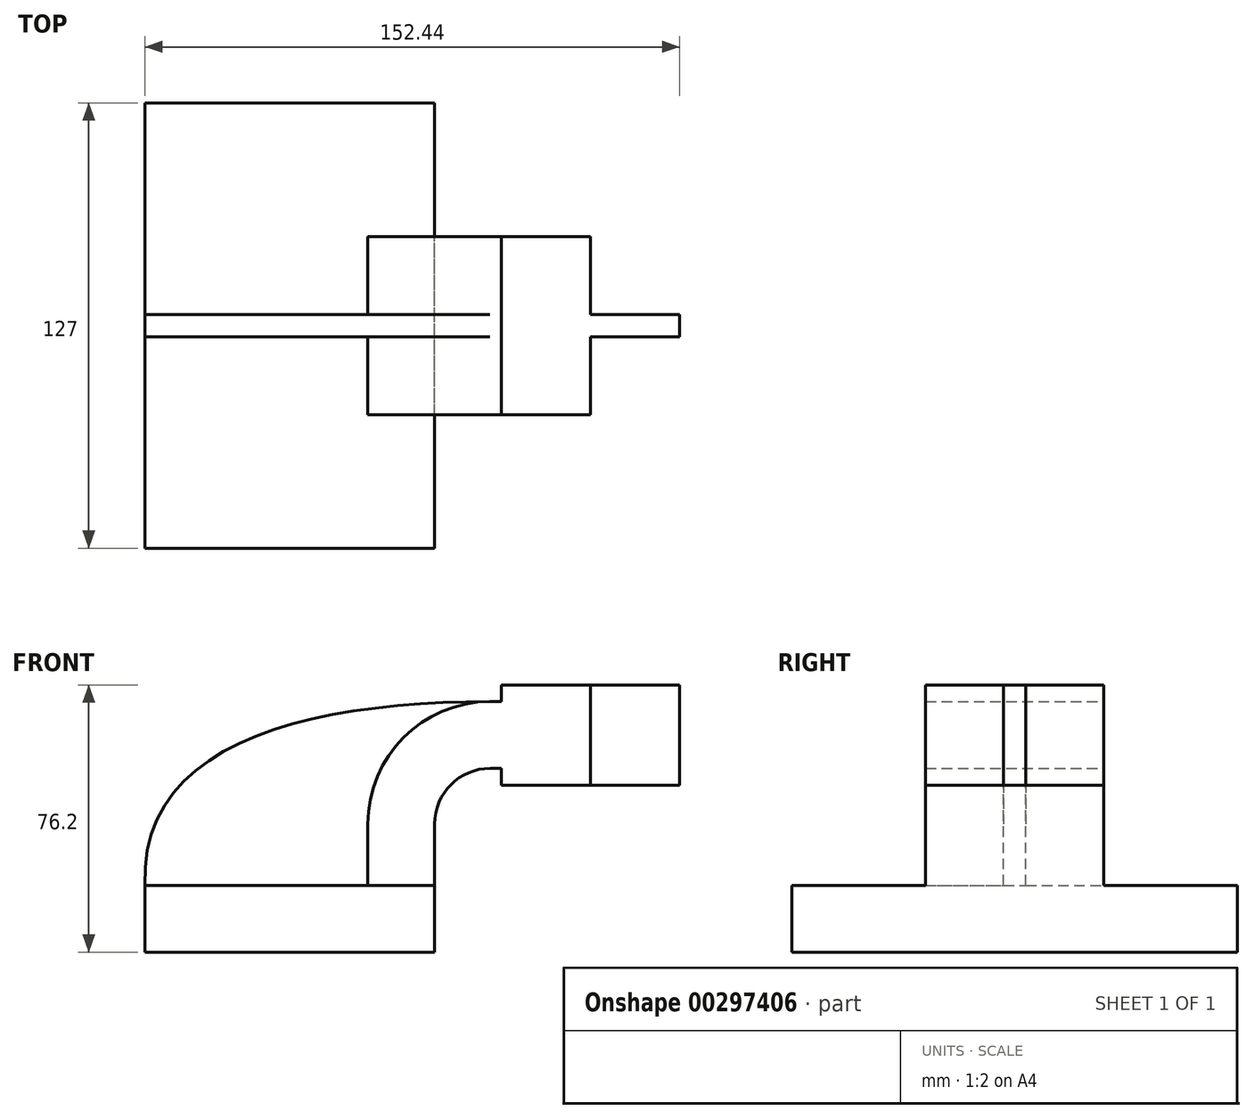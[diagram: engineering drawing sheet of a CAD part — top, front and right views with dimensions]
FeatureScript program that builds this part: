
annotation { "Feature Type Name" : "Feature", "Feature Type Description" : "" }
export const myFeature = defineFeature(function(context is Context, id is Id, definition is map)
    precondition{}
    {
        {
            var Q0;
            Q0=qCreatedBy(makeId("Front.planeOp"),FACE);
            var sketch = newSketch(context, id + "F0", { "sketchPlane" : qUnion([Q0])});
            skLineSegment(sketch, "E0.bottom", {"start": v(41.28, 9.53) * mm, "end": v(-41.28, 9.53) * mm});
            skLineSegment(sketch, "E0.top", {"start": v(41.28, -9.53) * mm, "end": v(-41.28, -9.53) * mm});
            skLineSegment(sketch, "E0.left", {"start": v(41.28, 9.53) * mm, "end": v(41.28, -9.53) * mm});
            skLineSegment(sketch, "E0.right", {"start": v(-41.28, 9.53) * mm, "end": v(-41.28, -9.53) * mm});
            skPoint(sketch, "E0.middle", {"position": v(0, 0) * mm});
            skLineSegment(sketch, "E1.bottom", {"start": v(111.12, 38.1) * mm, "end": v(60.33, 38.1) * mm});
            skLineSegment(sketch, "E1.top", {"start": v(111.13, 66.67) * mm, "end": v(60.33, 66.67) * mm});
            skLineSegment(sketch, "E1.left", {"start": v(111.12, 38.1) * mm, "end": v(111.12, 66.68) * mm});
            skLineSegment(sketch, "E1.right", {"start": v(60.33, 38.1) * mm, "end": v(60.33, 66.68) * mm});
            skPoint(sketch, "E1.middle", {"position": v(85.73, 52.39) * mm});
            skLineSegment(sketch, "E2", {"start": v(41.28, 9.53) * mm, "end": v(41.28, 27) * mm});
            skArc(sketch, "E3", {"start": v(41.28, 27) * mm, "mid": v(45.92, 38.23) * mm, "end": v(57.15, 42.88) * mm});
            skLineSegment(sketch, "E4", {"start": v(57.15, 42.88) * mm, "end": v(85.73, 42.88) * mm});
            skLineSegment(sketch, "E5.0", {"start": v(57.15, 61.93) * mm, "end": v(85.73, 61.93) * mm});
            skArc(sketch, "E5.1", {"start": v(22.23, 27) * mm, "mid": v(32.45, 51.7) * mm, "end": v(57.15, 61.93) * mm});
            skLineSegment(sketch, "E5.2", {"start": v(22.23, 9.53) * mm, "end": v(22.23, 27) * mm});
            skLineSegment(sketch, "E6", {"start": v(85.73, 38.1) * mm, "end": v(85.73, 66.67) * mm});
            skFitSpline(sketch, "E7", {"points": [v(-41.28, 9.52) * mm, v(57.15, 61.93) * mm], "startDerivative": vector(-5.3, 122.94) * mm, "endDerivative": vector(154.34, 0.3) * mm});
            skSolve(sketch);
        }
        {
            var Q0;
            Q0=makeQuery(id+"F0.imprint","IMPRINT",FACE,{"disambiguationData":[TD([[makeQuery(id+"F0.imprint","IMPRINT",EDGE,{"derivedFrom":sQuery(id+"F0.wireOp",EDGE,"E0.top")}),-1.0]])]});
            extrude(context, id + "F1", {"entities" : qUnion([Q0]), "endBound" : BoundingType.SYMMETRIC, "depth" : 127 * mm});
        }
        {
            var Q0;
            {var subQ1=sQuery(id+"F0.wireOp",EDGE,"E2");Q0=makeQuery(id+"F0.imprint","IMPRINT",FACE,{"disambiguationData":[TD([[makeQuery(id+"F0.imprint","IMPRINT",EDGE,{"derivedFrom":subQ1}),1.0]])]});}
            var Q1;
            {var subQ0=sQuery(id+"F0.wireOp",EDGE,"E4");var subQ1=sQuery(id+"F0.wireOp",EDGE,"E1.right");var subQ2=makeQuery(id+"F0.imprint","INTERSECT",VERTEX,{"derivedFrom":[subQ1,subQ0]});Q1=makeQuery(id+"F0.imprint","IMPRINT",FACE,{"disambiguationData":[TD([[makeQuery(id+"F0.imprint","IMPRINT",EDGE,{"disambiguationData":[TD([[subQ2,-1.0]])],"derivedFrom":subQ1}),-1.0]])]});}
            var Q2;
            {var subQ0=sQuery(id+"F0.wireOp",EDGE,"E1.right");var subQ1=sQuery(id+"F0.wireOp",EDGE,"E1.top");var subQ2=makeQuery(id+"F0.imprint","INTERSECT",VERTEX,{"derivedFrom":[subQ1,subQ0]});Q2=makeQuery(id+"F0.imprint","IMPRINT",FACE,{"disambiguationData":[TD([[makeQuery(id+"F0.imprint","IMPRINT",EDGE,{"disambiguationData":[TD([[subQ2,1.0]])],"derivedFrom":subQ1}),1.0]])]});}
            var Q3;
            {var subQ0=sQuery(id+"F0.wireOp",EDGE,"E1.right");var subQ1=sQuery(id+"F0.wireOp",EDGE,"E1.bottom");var subQ2=makeQuery(id+"F0.imprint","INTERSECT",VERTEX,{"derivedFrom":[subQ1,subQ0]});Q3=makeQuery(id+"F0.imprint","IMPRINT",FACE,{"disambiguationData":[TD([[makeQuery(id+"F0.imprint","IMPRINT",EDGE,{"disambiguationData":[TD([[subQ2,1.0]])],"derivedFrom":subQ1}),-1.0]])]});}
            extrude(context, id + "F2", {"entities" : qUnion([Q0, Q1, Q2, Q3]), "operationType" : NewBodyOperationType.ADD, "endBound" : BoundingType.SYMMETRIC, "depth" : 50.8 * mm});
        }
        {
            var Q0;
            Q0 = qSketchRegion(id + "F0", true);
            extrude(context, id + "F3", {"entities" : qUnion([Q0]), "operationType" : NewBodyOperationType.ADD, "endBound" : BoundingType.SYMMETRIC, "depth" : 6.35 * mm});
        }
    });
